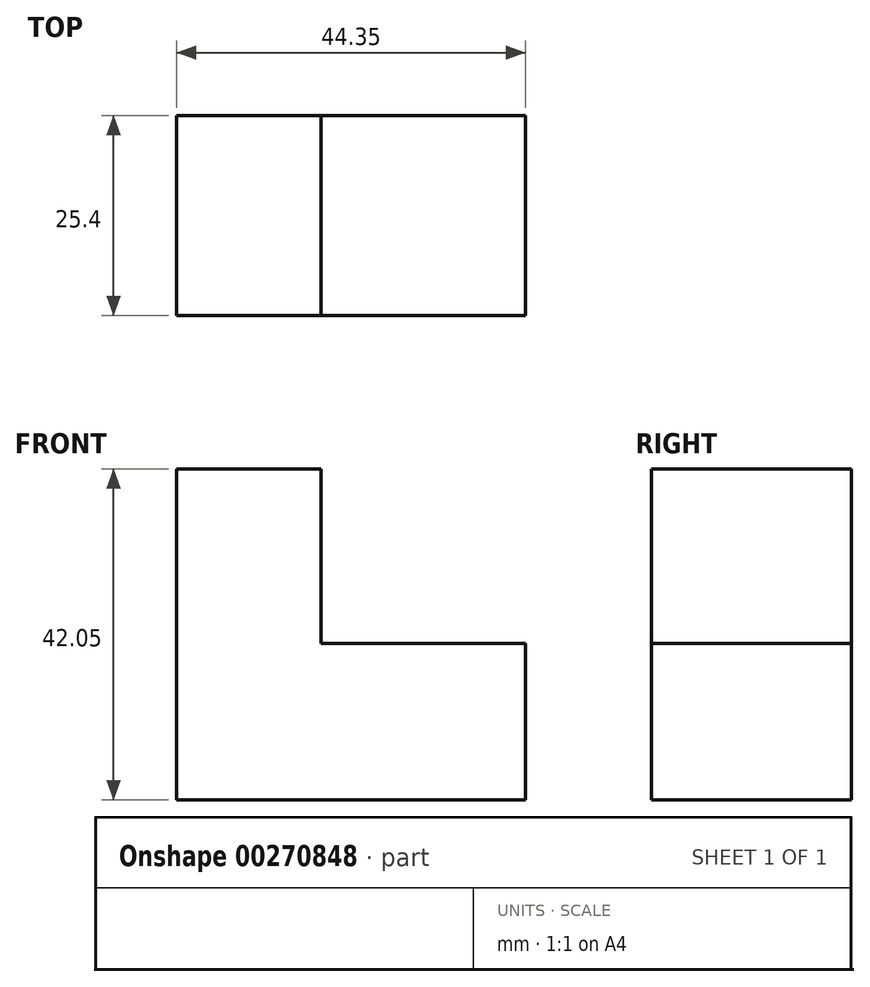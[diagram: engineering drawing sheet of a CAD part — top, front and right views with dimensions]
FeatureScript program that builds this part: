
annotation { "Feature Type Name" : "Feature", "Feature Type Description" : "" }
export const myFeature = defineFeature(function(context is Context, id is Id, definition is map)
    precondition{}
    {
        {
            var Q0;
            Q0=qCreatedBy(makeId("Front.planeOp"),FACE);
            var sketch = newSketch(context, id + "F0", { "sketchPlane" : qUnion([Q0])});
            skLineSegment(sketch, "E0", {"start": v(0, 0) * mm, "end": v(-44.35, 0) * mm});
            skLineSegment(sketch, "E1", {"start": v(-44.35, 0) * mm, "end": v(-44.35, 42.05) * mm});
            skLineSegment(sketch, "E2", {"start": v(-44.35, 42.05) * mm, "end": v(-25.97, 42.05) * mm});
            skLineSegment(sketch, "E3", {"start": v(-25.97, 42.05) * mm, "end": v(-25.97, 19.88) * mm});
            skLineSegment(sketch, "E4", {"start": v(-25.97, 19.88) * mm, "end": v(0, 19.88) * mm});
            skLineSegment(sketch, "E5", {"start": v(0, 19.88) * mm, "end": v(0, 0) * mm});
            skSolve(sketch);
        }
        {
            var Q0;
            Q0 = qSketchRegion(id + "F0", true);
            extrude(context, id + "F1", {"entities" : qUnion([Q0]), "depth" : 25.4 * mm});
        }
    });
